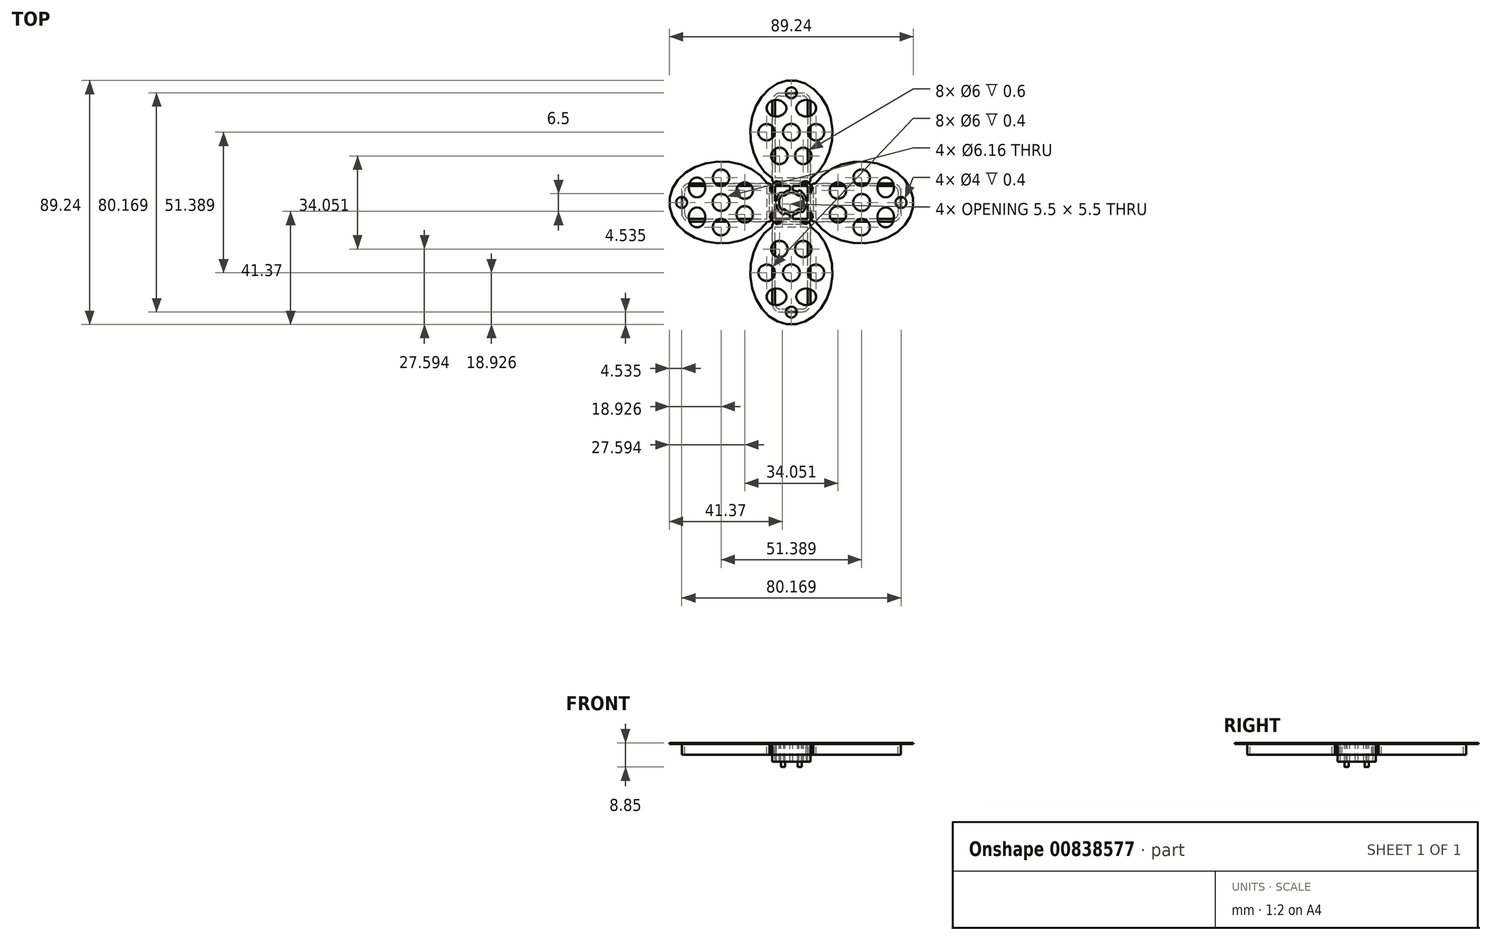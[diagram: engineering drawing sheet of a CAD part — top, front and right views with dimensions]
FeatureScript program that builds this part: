
annotation { "Feature Type Name" : "Feature", "Feature Type Description" : "" }
export const myFeature = defineFeature(function(context is Context, id is Id, definition is map)
    precondition{}
    {
        {
            var Q0;
            Q0=qCreatedBy(makeId("Top.planeOp"),FACE);
            var sketch = newSketch(context, id + "F0", { "sketchPlane" : qUnion([Q0])});
            skCircle(sketch, "E0", {"center": v(0, 0) * mm, "radius": 40 * mm, "construction": true});
            skLineSegment(sketch, "E1.bottom", {"start": v(40, 40) * mm, "end": v(-40, 40) * mm, "construction": true});
            skLineSegment(sketch, "E1.top", {"start": v(40, -40) * mm, "end": v(-40, -40) * mm, "construction": true});
            skLineSegment(sketch, "E1.left", {"start": v(40, 40) * mm, "end": v(40, -40) * mm, "construction": true});
            skLineSegment(sketch, "E1.right", {"start": v(-40, 40) * mm, "end": v(-40, -40) * mm, "construction": true});
            skLineSegment(sketch, "E2", {"start": v(0, 92.15) * mm, "end": v(0, -92.15) * mm, "construction": true});
            skLineSegment(sketch, "E3", {"start": v(-92.15, 0) * mm, "end": v(92.15, 0) * mm, "construction": true});
            skLineSegment(sketch, "E4", {"start": v(-92.15, 92.15) * mm, "end": v(92.15, -92.15) * mm, "construction": true});
            skLineSegment(sketch, "E5", {"start": v(92.15, 92.15) * mm, "end": v(-92.15, -92.15) * mm, "construction": true});
            skSolve(sketch);
        }
        {
            var Q0;
            Q0=qCreatedBy(makeId("Top.planeOp"),FACE);
            var sketch = newSketch(context, id + "F1", { "sketchPlane" : qUnion([Q0])});
            skLineSegment(sketch, "E6.bottom", {"start": v(7, 7) * mm, "end": v(-7, 7) * mm});
            skLineSegment(sketch, "E6.top", {"start": v(7, -7) * mm, "end": v(-7, -7) * mm});
            skLineSegment(sketch, "E6.left", {"start": v(7, 7) * mm, "end": v(7, -7) * mm});
            skLineSegment(sketch, "E6.right", {"start": v(-7, 7) * mm, "end": v(-7, -7) * mm});
            skPoint(sketch, "E6.middle", {"position": v(0, 0) * mm});
            skSolve(sketch);
        }
        {
            var Q0;
            Q0 = qSketchRegion(id + "F1", true);
            extrude(context, id + "F2", {"entities" : qUnion([Q0]), "oppositeDirection" : true, "depth" : 6.45 * mm, "offsetDistance" : 25 * mm});
        }
        {
            var Q0;
            Q0=qCreatedBy(makeId("Top.planeOp"),FACE);
            var sketch = newSketch(context, id + "F3", { "sketchPlane" : qUnion([Q0])});
            skLineSegment(sketch, "E7.bottom", {"start": v(7, 7) * mm, "end": v(-7, 7) * mm});
            skLineSegment(sketch, "E7.top", {"start": v(7, 40) * mm, "end": v(-7, 40) * mm});
            skLineSegment(sketch, "E7.left", {"start": v(7, 7) * mm, "end": v(7, 40) * mm});
            skLineSegment(sketch, "E7.right", {"start": v(-7, 7) * mm, "end": v(-7, 40) * mm});
            skPoint(sketch, "E7.middle", {"position": v(0, 23.5) * mm});
            skLineSegment(sketch, "E8.1.0", {"start": v(-7, 7) * mm, "end": v(-40, 7) * mm});
            skLineSegment(sketch, "E8.1.1", {"start": v(-7, 7) * mm, "end": v(-7, -7) * mm});
            skPoint(sketch, "E8.1.2", {"position": v(-23.5, 0) * mm});
            skLineSegment(sketch, "E8.1.3", {"start": v(-7, -7) * mm, "end": v(-40, -7) * mm});
            skLineSegment(sketch, "E8.1.4", {"start": v(-40, 7) * mm, "end": v(-40, -7) * mm});
            skLineSegment(sketch, "E8.2.0", {"start": v(-7, -7) * mm, "end": v(-7, -40) * mm});
            skLineSegment(sketch, "E8.2.1", {"start": v(-7, -7) * mm, "end": v(7, -7) * mm});
            skPoint(sketch, "E8.2.2", {"position": v(0, -23.5) * mm});
            skLineSegment(sketch, "E8.2.3", {"start": v(7, -7) * mm, "end": v(7, -40) * mm});
            skLineSegment(sketch, "E8.2.4", {"start": v(-7, -40) * mm, "end": v(7, -40) * mm});
            skLineSegment(sketch, "E8.3.0", {"start": v(7, -7) * mm, "end": v(40, -7) * mm});
            skLineSegment(sketch, "E8.3.1", {"start": v(7, -7) * mm, "end": v(7, 7) * mm});
            skPoint(sketch, "E8.3.2", {"position": v(23.5, 0) * mm});
            skLineSegment(sketch, "E8.3.3", {"start": v(7, 7) * mm, "end": v(40, 7) * mm});
            skLineSegment(sketch, "E8.3.4", {"start": v(40, -7) * mm, "end": v(40, 7) * mm});
            skPoint(sketch, "E8.center", {"position": v(0, 0) * mm});
            skSolve(sketch);
        }
        {
            var Q0;
            Q0 = qSketchRegion(id + "F3", true);
            extrude(context, id + "F4", {"entities" : qUnion([Q0]), "operationType" : NewBodyOperationType.ADD, "oppositeDirection" : true, "depth" : .2 * mm, "offsetDistance" : 25 * mm});
        }
        {
            var Q0;
            Q0=qCreatedBy(makeId("Top.planeOp"),FACE);
            var sketch = newSketch(context, id + "F5", { "sketchPlane" : qUnion([Q0])});
            skLineSegment(sketch, "E9.bottom", {"start": v(-7, -8) * mm, "end": v(-4.5, -8) * mm});
            skLineSegment(sketch, "E9.top", {"start": v(-7, -7) * mm, "end": v(-4.5, -7) * mm});
            skLineSegment(sketch, "E9.left", {"start": v(-7, -8) * mm, "end": v(-7, -7) * mm});
            skLineSegment(sketch, "E9.right", {"start": v(-4.5, -8) * mm, "end": v(-4.5, -7) * mm});
            skLineSegment(sketch, "E10.MirrorCS", {"start": v(7, -8) * mm, "end": v(4.5, -8) * mm});
            skLineSegment(sketch, "E11.MirrorCS", {"start": v(4.5, -8) * mm, "end": v(4.5, -7) * mm});
            skLineSegment(sketch, "E12.MirrorCS", {"start": v(7, -7) * mm, "end": v(4.5, -7) * mm});
            skLineSegment(sketch, "E13.MirrorCS", {"start": v(7, -8) * mm, "end": v(7, -7) * mm});
            skLineSegment(sketch, "E14.1.0", {"start": v(7, 7) * mm, "end": v(7, 4.5) * mm});
            skLineSegment(sketch, "E14.1.1", {"start": v(7, -7) * mm, "end": v(7, -4.5) * mm});
            skLineSegment(sketch, "E14.1.2", {"start": v(8, 4.5) * mm, "end": v(7, 4.5) * mm});
            skLineSegment(sketch, "E14.1.3", {"start": v(8, -7) * mm, "end": v(7, -7) * mm});
            skLineSegment(sketch, "E14.1.4", {"start": v(8, 7) * mm, "end": v(8, 4.5) * mm});
            skLineSegment(sketch, "E14.1.5", {"start": v(8, 7) * mm, "end": v(7, 7) * mm});
            skLineSegment(sketch, "E14.1.6", {"start": v(8, -4.5) * mm, "end": v(7, -4.5) * mm});
            skLineSegment(sketch, "E14.1.7", {"start": v(8, -7) * mm, "end": v(8, -4.5) * mm});
            skLineSegment(sketch, "E14.2.0", {"start": v(-7, 7) * mm, "end": v(-4.5, 7) * mm});
            skLineSegment(sketch, "E14.2.1", {"start": v(7, 7) * mm, "end": v(4.5, 7) * mm});
            skLineSegment(sketch, "E14.2.2", {"start": v(-4.5, 8) * mm, "end": v(-4.5, 7) * mm});
            skLineSegment(sketch, "E14.2.3", {"start": v(7, 8) * mm, "end": v(7, 7) * mm});
            skLineSegment(sketch, "E14.2.4", {"start": v(-7, 8) * mm, "end": v(-4.5, 8) * mm});
            skLineSegment(sketch, "E14.2.5", {"start": v(-7, 8) * mm, "end": v(-7, 7) * mm});
            skLineSegment(sketch, "E14.2.6", {"start": v(4.5, 8) * mm, "end": v(4.5, 7) * mm});
            skLineSegment(sketch, "E14.2.7", {"start": v(7, 8) * mm, "end": v(4.5, 8) * mm});
            skLineSegment(sketch, "E14.3.0", {"start": v(-7, -7) * mm, "end": v(-7, -4.5) * mm});
            skLineSegment(sketch, "E14.3.1", {"start": v(-7, 7) * mm, "end": v(-7, 4.5) * mm});
            skLineSegment(sketch, "E14.3.2", {"start": v(-8, -4.5) * mm, "end": v(-7, -4.5) * mm});
            skLineSegment(sketch, "E14.3.3", {"start": v(-8, 7) * mm, "end": v(-7, 7) * mm});
            skLineSegment(sketch, "E14.3.4", {"start": v(-8, -7) * mm, "end": v(-8, -4.5) * mm});
            skLineSegment(sketch, "E14.3.5", {"start": v(-8, -7) * mm, "end": v(-7, -7) * mm});
            skLineSegment(sketch, "E14.3.6", {"start": v(-8, 4.5) * mm, "end": v(-7, 4.5) * mm});
            skLineSegment(sketch, "E14.3.7", {"start": v(-8, 7) * mm, "end": v(-8, 4.5) * mm});
            skPoint(sketch, "E14.center", {"position": v(0, 0) * mm});
            skSolve(sketch);
        }
        {
            var Q0;
            Q0 = qSketchRegion(id + "F5", true);
            var Q1;
            {var subQ0=sQuery(id+"F3.wireOp",EDGE,"E8.2.0");var subQ2=sQuery(id+"F3.wireOp",EDGE,"E8.1.3");var subQ4=sQuery(id+"F3.wireOp",EDGE,"E8.1.0");var subQ6=makeQuery(id+"F2.opExtrude","SWEPT_FACE",FACE,{"disambiguationData":[OSD([sQuery(id+"F1.wireOp",EDGE,"E6.bottom")])]});var subQ7=sQuery(id+"F3.wireOp",EDGE,"E7.right");var subQ10=sQuery(id+"F3.wireOp",EDGE,"E8.1.4");var subQ11=makeQuery(id+"F4.opExtrude","CAP_FACE",FACE,{"disambiguationData":[OSD([sQuery(id+"F3.wireOp",EDGE,"E7.top"),sQuery(id+"F3.wireOp",EDGE,"E7.left"),subQ7,subQ4,subQ2,subQ10,subQ0,sQuery(id+"F3.wireOp",EDGE,"E8.2.3"),sQuery(id+"F3.wireOp",EDGE,"E8.2.4"),sQuery(id+"F3.wireOp",EDGE,"E8.3.0"),sQuery(id+"F3.wireOp",EDGE,"E8.3.3"),sQuery(id+"F3.wireOp",EDGE,"E8.3.4")])],"isStart":false});Q1=makeQuery(id+"F11.boolean.opBoolean","SPLIT",FACE,{"disambiguationData":[TD([subQ6])],"derivedFrom":makeQuery(id+"F4.boolean.opBoolean","SPLIT",FACE,{"disambiguationData":[TD([makeQuery(id+"F4.opExtrude","SWEPT_FACE",FACE,{"disambiguationData":[OSD([subQ10])]})])],"derivedFrom":subQ11})});}
            extrude(context, id + "F6", {"entities" : qUnion([Q0]), "operationType" : NewBodyOperationType.REMOVE, "endBound" : BoundingType.UP_TO_SURFACE, "oppositeDirection" : true, "depth" : 25 * mm, "endBoundEntityFace" : qUnion([Q1]), "offsetDistance" : 25 * mm});
        }
        {
            var Q0;
            Q0=qCreatedBy(makeId("Top.planeOp"),FACE);
            var sketch = newSketch(context, id + "F7", { "sketchPlane" : qUnion([Q0])});
            skEllipse(sketch, "E15", {"center": v(0, 25.62) * mm, "majorRadius": 16.56 * mm, "minorRadius": 14.13 * mm, "majorAxis": v(0, 1)});
            skEllipse(sketch, "E16.1.0", {"center": v(-25.62, 0) * mm, "majorRadius": 16.56 * mm, "minorRadius": 14.13 * mm, "majorAxis": v(-1, 0)});
            skEllipse(sketch, "E16.2.0", {"center": v(0, -25.62) * mm, "majorRadius": 16.56 * mm, "minorRadius": 14.13 * mm, "majorAxis": v(0, -1)});
            skEllipse(sketch, "E16.3.0", {"center": v(25.62, 0) * mm, "majorRadius": 16.56 * mm, "minorRadius": 14.13 * mm, "majorAxis": v(1, 0)});
            skPoint(sketch, "E16.center", {"position": v(0, 0) * mm});
            skLineSegment(sketch, "E17", {"start": v(-17.7, 25.62) * mm, "end": v(18.9, 25.62) * mm, "construction": true});
            skSolve(sketch);
        }
        {
            var Q0;
            Q0=qCreatedBy(makeId("Top.planeOp"),FACE);
            var sketch = newSketch(context, id + "F8", { "sketchPlane" : qUnion([Q0])});
            skCircle(sketch, "E18", {"center": v(-9.03, 25.7) * mm, "radius": 3 * mm});
            skArc(sketch, "E19", {"start": v(-6.35, 14.78) * mm, "mid": v(-1.36, 17.03) * mm, "end": v(-6.35, 19.27) * mm});
            skArc(sketch, "E20.MirrorC", {"start": v(6.35, 14.78) * mm, "mid": v(1.36, 17.03) * mm, "end": v(6.35, 19.27) * mm});
            skCircle(sketch, "E21.MirrorC", {"center": v(9.03, 25.7) * mm, "radius": 3 * mm});
            skCircle(sketch, "E22", {"center": v(0, 25.7) * mm, "radius": 3.08 * mm});
            skEllipse(sketch, "E23", {"center": v(-5.46, 34.49) * mm, "majorRadius": 3.63 * mm, "minorRadius": 3.04 * mm, "majorAxis": v(1, 0)});
            skEllipse(sketch, "E24.MirrorC", {"center": v(5.46, 34.49) * mm, "majorRadius": 3.63 * mm, "minorRadius": 3.04 * mm, "majorAxis": v(-1, 0)});
            skEllipse(sketch, "E25.MirrorC", {"center": v(5.46, 34.49) * mm, "majorRadius": 3.63 * mm, "minorRadius": 3.04 * mm, "majorAxis": v(-1, 0)});
            skLineSegment(sketch, "E26.left", {"start": v(6.35, 19.27) * mm, "end": v(6.35, 14.78) * mm});
            skLineSegment(sketch, "E26.right", {"start": v(-6.35, 19.27) * mm, "end": v(-6.35, 14.78) * mm});
            skPoint(sketch, "E26.middle", {"position": v(0, 16.86) * mm});
            skPoint(sketch, "E26.bottom.start.orphan", {"position": v(6.35, 20.86) * mm});
            skPoint(sketch, "E27.orphan", {"position": v(-6.35, 20.86) * mm});
            skPoint(sketch, "E28.orphan", {"position": v(-6.35, 12.86) * mm});
            skPoint(sketch, "E29.orphan", {"position": v(6.35, 12.86) * mm});
            skPoint(sketch, "E30.1.0", {"position": v(-16.86, 0) * mm});
            skArc(sketch, "E30.1.1", {"start": v(-14.78, -6.35) * mm, "mid": v(-17.03, -1.36) * mm, "end": v(-19.27, -6.35) * mm});
            skPoint(sketch, "E30.1.2", {"position": v(-20.86, 6.35) * mm});
            skEllipse(sketch, "E30.1.3", {"center": v(-34.49, -5.46) * mm, "majorRadius": 3.63 * mm, "minorRadius": 3.04 * mm, "majorAxis": v(0, 1)});
            skEllipse(sketch, "E30.1.4", {"center": v(-34.49, 5.46) * mm, "majorRadius": 3.63 * mm, "minorRadius": 3.04 * mm, "majorAxis": v(0, -1)});
            skPoint(sketch, "E30.1.5", {"position": v(-12.86, 6.35) * mm});
            skCircle(sketch, "E30.1.6", {"center": v(-25.7, 9.03) * mm, "radius": 3 * mm});
            skLineSegment(sketch, "E30.1.7", {"start": v(-19.27, 6.35) * mm, "end": v(-14.78, 6.35) * mm});
            skPoint(sketch, "E30.1.8", {"position": v(-12.86, -6.35) * mm});
            skLineSegment(sketch, "E30.1.9", {"start": v(-19.27, -6.35) * mm, "end": v(-14.78, -6.35) * mm});
            skCircle(sketch, "E30.1.10", {"center": v(-25.7, -9.03) * mm, "radius": 3 * mm});
            skPoint(sketch, "E30.1.11", {"position": v(-20.86, -6.35) * mm});
            skCircle(sketch, "E30.1.12", {"center": v(-25.7, 0) * mm, "radius": 3.08 * mm});
            skArc(sketch, "E30.1.13", {"start": v(-14.78, 6.35) * mm, "mid": v(-17.03, 1.36) * mm, "end": v(-19.27, 6.35) * mm});
            skEllipse(sketch, "E30.1.14", {"center": v(-34.49, 5.46) * mm, "majorRadius": 3.63 * mm, "minorRadius": 3.04 * mm, "majorAxis": v(0, -1)});
            skPoint(sketch, "E30.2.0", {"position": v(0, -16.86) * mm});
            skArc(sketch, "E30.2.1", {"start": v(6.35, -14.78) * mm, "mid": v(1.36, -17.03) * mm, "end": v(6.35, -19.27) * mm});
            skPoint(sketch, "E30.2.2", {"position": v(-6.35, -20.86) * mm});
            skEllipse(sketch, "E30.2.3", {"center": v(5.46, -34.49) * mm, "majorRadius": 3.63 * mm, "minorRadius": 3.04 * mm, "majorAxis": v(-1, 0)});
            skEllipse(sketch, "E30.2.4", {"center": v(-5.46, -34.49) * mm, "majorRadius": 3.63 * mm, "minorRadius": 3.04 * mm, "majorAxis": v(1, 0)});
            skPoint(sketch, "E30.2.5", {"position": v(-6.35, -12.86) * mm});
            skCircle(sketch, "E30.2.6", {"center": v(-9.03, -25.7) * mm, "radius": 3 * mm});
            skLineSegment(sketch, "E30.2.7", {"start": v(-6.35, -19.27) * mm, "end": v(-6.35, -14.78) * mm});
            skPoint(sketch, "E30.2.8", {"position": v(6.35, -12.86) * mm});
            skLineSegment(sketch, "E30.2.9", {"start": v(6.35, -19.27) * mm, "end": v(6.35, -14.78) * mm});
            skCircle(sketch, "E30.2.10", {"center": v(9.03, -25.7) * mm, "radius": 3 * mm});
            skPoint(sketch, "E30.2.11", {"position": v(6.35, -20.86) * mm});
            skCircle(sketch, "E30.2.12", {"center": v(0, -25.7) * mm, "radius": 3.08 * mm});
            skArc(sketch, "E30.2.13", {"start": v(-6.35, -14.78) * mm, "mid": v(-1.36, -17.03) * mm, "end": v(-6.35, -19.27) * mm});
            skEllipse(sketch, "E30.2.14", {"center": v(-5.46, -34.49) * mm, "majorRadius": 3.63 * mm, "minorRadius": 3.04 * mm, "majorAxis": v(1, 0)});
            skPoint(sketch, "E30.3.0", {"position": v(16.86, 0) * mm});
            skArc(sketch, "E30.3.1", {"start": v(14.78, 6.35) * mm, "mid": v(17.03, 1.36) * mm, "end": v(19.27, 6.35) * mm});
            skPoint(sketch, "E30.3.2", {"position": v(20.86, -6.35) * mm});
            skEllipse(sketch, "E30.3.3", {"center": v(34.49, 5.46) * mm, "majorRadius": 3.63 * mm, "minorRadius": 3.04 * mm, "majorAxis": v(0, -1)});
            skEllipse(sketch, "E30.3.4", {"center": v(34.49, -5.46) * mm, "majorRadius": 3.63 * mm, "minorRadius": 3.04 * mm, "majorAxis": v(0, 1)});
            skPoint(sketch, "E30.3.5", {"position": v(12.86, -6.35) * mm});
            skCircle(sketch, "E30.3.6", {"center": v(25.7, -9.03) * mm, "radius": 3 * mm});
            skLineSegment(sketch, "E30.3.7", {"start": v(19.27, -6.35) * mm, "end": v(14.78, -6.35) * mm});
            skPoint(sketch, "E30.3.8", {"position": v(12.86, 6.35) * mm});
            skLineSegment(sketch, "E30.3.9", {"start": v(19.27, 6.35) * mm, "end": v(14.78, 6.35) * mm});
            skCircle(sketch, "E30.3.10", {"center": v(25.7, 9.03) * mm, "radius": 3 * mm});
            skPoint(sketch, "E30.3.11", {"position": v(20.86, 6.35) * mm});
            skCircle(sketch, "E30.3.12", {"center": v(25.7, 0) * mm, "radius": 3.08 * mm});
            skArc(sketch, "E30.3.13", {"start": v(14.78, -6.35) * mm, "mid": v(17.03, -1.36) * mm, "end": v(19.27, -6.35) * mm});
            skEllipse(sketch, "E30.3.14", {"center": v(34.49, -5.46) * mm, "majorRadius": 3.63 * mm, "minorRadius": 3.04 * mm, "majorAxis": v(0, 1)});
            skPoint(sketch, "E30.center", {"position": v(0, 0) * mm});
            skSolve(sketch);
        }
        {
            var Q0;
            Q0 = qSketchRegion(id + "F8", true);
            var Q1;
            {var subQ0=sQuery(id+"F3.wireOp",EDGE,"E7.top");var subQ1=sQuery(id+"F3.wireOp",EDGE,"E7.left");var subQ2=sQuery(id+"F3.wireOp",EDGE,"E7.right");var subQ3=sQuery(id+"F3.wireOp",EDGE,"E8.3.3");var subQ4=sQuery(id+"F3.wireOp",EDGE,"E8.1.0");var subQ5=makeQuery(id+"F4.opExtrude","CAP_FACE",FACE,{"disambiguationData":[OSD([subQ0,subQ1,subQ2,subQ4,sQuery(id+"F3.wireOp",EDGE,"E8.1.3"),sQuery(id+"F3.wireOp",EDGE,"E8.1.4"),sQuery(id+"F3.wireOp",EDGE,"E8.2.0"),sQuery(id+"F3.wireOp",EDGE,"E8.2.3"),sQuery(id+"F3.wireOp",EDGE,"E8.2.4"),sQuery(id+"F3.wireOp",EDGE,"E8.3.0"),subQ3,sQuery(id+"F3.wireOp",EDGE,"E8.3.4")])],"isStart":false});Q1=makeQuery(id+"FxwcccIiPXIM7xx_1.boolean.opBoolean","MERGE",FACE,{"derivedFrom":[makeQuery(id+"F4.boolean.opBoolean","SPLIT",FACE,{"disambiguationData":[TD([makeQuery(id+"F4.opExtrude","SWEPT_FACE",FACE,{"disambiguationData":[OSD([subQ0])]})])],"derivedFrom":subQ5}),makeQuery(id+"FxwcccIiPXIM7xx_1.opExtrude","CAP_FACE",FACE,{"disambiguationData":[OSD([sQuery(id+"F7.wireOp",EDGE,"E15")])],"isStart":false})]});}
            extrude(context, id + "F9", {"entities" : qUnion([Q0]), "operationType" : NewBodyOperationType.REMOVE, "endBound" : BoundingType.UP_TO_SURFACE, "oppositeDirection" : true, "depth" : 25 * mm, "endBoundEntityFace" : qUnion([Q1]), "offsetDistance" : 25 * mm});
        }
        {
            var Q0;
            Q0=qCreatedBy(makeId("Top.planeOp"),FACE);
            var sketch = newSketch(context, id + "F10", { "sketchPlane" : qUnion([Q0])});
            skLineSegment(sketch, "E31.left", {"start": v(-7, -40) * mm, "end": v(-7, -8) * mm});
            skLineSegment(sketch, "E31.right", {"start": v(-6, -39) * mm, "end": v(-6, -9) * mm});
            skLineSegment(sketch, "E32.top", {"start": v(-6, -39) * mm, "end": v(0, -39) * mm});
            skLineSegment(sketch, "E33.top", {"start": v(-6, -9) * mm, "end": v(0, -9) * mm});
            skLineSegment(sketch, "E34", {"start": v(-7, -8) * mm, "end": v(-6.2, -7.2) * mm});
            skLineSegment(sketch, "E35", {"start": v(-6.2, -7.2) * mm, "end": v(-5.4, -8) * mm});
            skLineSegment(sketch, "E36.trimOffspring", {"start": v(-5.4, -8) * mm, "end": v(0, -8) * mm});
            skLineSegment(sketch, "E37", {"start": v(-7, -40) * mm, "end": v(0, -40) * mm});
            skLineSegment(sketch, "E38.MirrorCS", {"start": v(7, -8) * mm, "end": v(6.2, -7.2) * mm});
            skLineSegment(sketch, "E39.MirrorCS", {"start": v(7, -40) * mm, "end": v(7, -8) * mm});
            skLineSegment(sketch, "E40.MirrorCS", {"start": v(6, -39) * mm, "end": v(6, -9) * mm});
            skLineSegment(sketch, "E41.MirrorCS", {"start": v(5.4, -8) * mm, "end": v(0, -8) * mm});
            skLineSegment(sketch, "E42.MirrorCS", {"start": v(6.2, -7.2) * mm, "end": v(5.4, -8) * mm});
            skLineSegment(sketch, "E43.MirrorCS", {"start": v(7, -40) * mm, "end": v(0, -40) * mm});
            skLineSegment(sketch, "E44.MirrorCS", {"start": v(6, -9) * mm, "end": v(0, -9) * mm});
            skLineSegment(sketch, "E45.MirrorCS", {"start": v(6, -39) * mm, "end": v(0, -39) * mm});
            skLineSegment(sketch, "E46.1.0", {"start": v(8, -5.4) * mm, "end": v(8, 0) * mm});
            skLineSegment(sketch, "E46.1.1", {"start": v(40, 7) * mm, "end": v(8, 7) * mm});
            skLineSegment(sketch, "E46.1.2", {"start": v(8, 5.4) * mm, "end": v(8, 0) * mm});
            skLineSegment(sketch, "E46.1.3", {"start": v(40, -7) * mm, "end": v(8, -7) * mm});
            skLineSegment(sketch, "E46.1.4", {"start": v(39, -6) * mm, "end": v(9, -6) * mm});
            skLineSegment(sketch, "E46.1.5", {"start": v(9, 6) * mm, "end": v(9, 0) * mm});
            skLineSegment(sketch, "E46.1.6", {"start": v(39, 6) * mm, "end": v(9, 6) * mm});
            skLineSegment(sketch, "E46.1.7", {"start": v(40, 7) * mm, "end": v(40, 0) * mm});
            skLineSegment(sketch, "E46.1.8", {"start": v(39, 6) * mm, "end": v(39, 0) * mm});
            skLineSegment(sketch, "E46.1.9", {"start": v(9, -6) * mm, "end": v(9, 0) * mm});
            skLineSegment(sketch, "E46.1.10", {"start": v(39, -6) * mm, "end": v(39, 0) * mm});
            skLineSegment(sketch, "E46.1.11", {"start": v(40, -7) * mm, "end": v(40, 0) * mm});
            skLineSegment(sketch, "E46.1.12", {"start": v(7.2, 6.2) * mm, "end": v(8, 5.4) * mm});
            skLineSegment(sketch, "E46.1.13", {"start": v(8, -7) * mm, "end": v(7.2, -6.2) * mm});
            skLineSegment(sketch, "E46.1.14", {"start": v(8, 7) * mm, "end": v(7.2, 6.2) * mm});
            skLineSegment(sketch, "E46.1.15", {"start": v(7.2, -6.2) * mm, "end": v(8, -5.4) * mm});
            skLineSegment(sketch, "E46.2.0", {"start": v(5.4, 8) * mm, "end": v(0, 8) * mm});
            skLineSegment(sketch, "E46.2.1", {"start": v(-7, 40) * mm, "end": v(-7, 8) * mm});
            skLineSegment(sketch, "E46.2.2", {"start": v(-5.4, 8) * mm, "end": v(0, 8) * mm});
            skLineSegment(sketch, "E46.2.3", {"start": v(7, 40) * mm, "end": v(7, 8) * mm});
            skLineSegment(sketch, "E46.2.4", {"start": v(6, 39) * mm, "end": v(6, 9) * mm});
            skLineSegment(sketch, "E46.2.5", {"start": v(-6, 9) * mm, "end": v(0, 9) * mm});
            skLineSegment(sketch, "E46.2.6", {"start": v(-6, 39) * mm, "end": v(-6, 9) * mm});
            skLineSegment(sketch, "E46.2.7", {"start": v(-7, 40) * mm, "end": v(0, 40) * mm});
            skLineSegment(sketch, "E46.2.8", {"start": v(-6, 39) * mm, "end": v(0, 39) * mm});
            skLineSegment(sketch, "E46.2.9", {"start": v(6, 9) * mm, "end": v(0, 9) * mm});
            skLineSegment(sketch, "E46.2.10", {"start": v(6, 39) * mm, "end": v(0, 39) * mm});
            skLineSegment(sketch, "E46.2.11", {"start": v(7, 40) * mm, "end": v(0, 40) * mm});
            skLineSegment(sketch, "E46.2.12", {"start": v(-6.2, 7.2) * mm, "end": v(-5.4, 8) * mm});
            skLineSegment(sketch, "E46.2.13", {"start": v(7, 8) * mm, "end": v(6.2, 7.2) * mm});
            skLineSegment(sketch, "E46.2.14", {"start": v(-7, 8) * mm, "end": v(-6.2, 7.2) * mm});
            skLineSegment(sketch, "E46.2.15", {"start": v(6.2, 7.2) * mm, "end": v(5.4, 8) * mm});
            skLineSegment(sketch, "E46.3.0", {"start": v(-8, 5.4) * mm, "end": v(-8, 0) * mm});
            skLineSegment(sketch, "E46.3.1", {"start": v(-40, -7) * mm, "end": v(-8, -7) * mm});
            skLineSegment(sketch, "E46.3.2", {"start": v(-8, -5.4) * mm, "end": v(-8, 0) * mm});
            skLineSegment(sketch, "E46.3.3", {"start": v(-40, 7) * mm, "end": v(-8, 7) * mm});
            skLineSegment(sketch, "E46.3.4", {"start": v(-39, 6) * mm, "end": v(-9, 6) * mm});
            skLineSegment(sketch, "E46.3.5", {"start": v(-9, -6) * mm, "end": v(-9, 0) * mm});
            skLineSegment(sketch, "E46.3.6", {"start": v(-39, -6) * mm, "end": v(-9, -6) * mm});
            skLineSegment(sketch, "E46.3.7", {"start": v(-40, -7) * mm, "end": v(-40, 0) * mm});
            skLineSegment(sketch, "E46.3.8", {"start": v(-39, -6) * mm, "end": v(-39, 0) * mm});
            skLineSegment(sketch, "E46.3.9", {"start": v(-9, 6) * mm, "end": v(-9, 0) * mm});
            skLineSegment(sketch, "E46.3.10", {"start": v(-39, 6) * mm, "end": v(-39, 0) * mm});
            skLineSegment(sketch, "E46.3.11", {"start": v(-40, 7) * mm, "end": v(-40, 0) * mm});
            skLineSegment(sketch, "E46.3.12", {"start": v(-7.2, -6.2) * mm, "end": v(-8, -5.4) * mm});
            skLineSegment(sketch, "E46.3.13", {"start": v(-8, 7) * mm, "end": v(-7.2, 6.2) * mm});
            skLineSegment(sketch, "E46.3.14", {"start": v(-8, -7) * mm, "end": v(-7.2, -6.2) * mm});
            skLineSegment(sketch, "E46.3.15", {"start": v(-7.2, 6.2) * mm, "end": v(-8, 5.4) * mm});
            skPoint(sketch, "E46.center", {"position": v(0, 0) * mm});
            skSolve(sketch);
        }
        {
            var Q0;
            Q0 = qSketchRegion(id + "F10", true);
            extrude(context, id + "F11", {"entities" : qUnion([Q0]), "operationType" : NewBodyOperationType.ADD, "oppositeDirection" : true, "depth" : 4 * mm, "offsetDistance" : 25 * mm});
        }
        {
            var Q0;
            Q0=qCreatedBy(makeId("Top.planeOp"),FACE);
            var sketch = newSketch(context, id + "F12", { "sketchPlane" : qUnion([Q0])});
            skArc(sketch, "E47", {"start": v(-2.45, -2.5) * mm, "mid": v(0, -3.5) * mm, "end": v(2.45, -2.5) * mm});
            skArc(sketch, "E48", {"start": v(-3.74, 2.5) * mm, "mid": v(-4.5, 0) * mm, "end": v(-3.74, -2.5) * mm});
            skLineSegment(sketch, "E49.bottom", {"start": v(3.74, 2.5) * mm, "end": v(2.45, 2.5) * mm});
            skLineSegment(sketch, "E49.top", {"start": v(3.74, -2.5) * mm, "end": v(2.45, -2.5) * mm});
            skArc(sketch, "E50.trimOffspring", {"start": v(2.45, 2.5) * mm, "mid": v(0, 3.5) * mm, "end": v(-2.45, 2.5) * mm});
            skArc(sketch, "E51.trimOffspring", {"start": v(3.74, -2.5) * mm, "mid": v(4.5, 0) * mm, "end": v(3.74, 2.5) * mm});
            skLineSegment(sketch, "E52.trimOffspring", {"start": v(-2.45, -2.5) * mm, "end": v(-3.74, -2.5) * mm});
            skLineSegment(sketch, "E53.trimOffspring", {"start": v(-2.45, 2.5) * mm, "end": v(-3.74, 2.5) * mm});
            skSolve(sketch);
        }
        {
            var Q0;
            Q0 = qSketchRegion(id + "F12", true);
            var Q1;
            Q1=makeQuery(id+"F2.opExtrude","CAP_FACE",FACE,{"disambiguationData":[OSD([sQuery(id+"F1.wireOp",EDGE,"E6.bottom"),sQuery(id+"F1.wireOp",EDGE,"E6.top"),sQuery(id+"F1.wireOp",EDGE,"E6.left"),sQuery(id+"F1.wireOp",EDGE,"E6.right")])],"isStart":false});
            var Q2;
            Q2=makeQuery(id+"F4.opExtrude","CAP_FACE",FACE,{"disambiguationData":[OSD([sQuery(id+"F3.wireOp",EDGE,"E7.top"),sQuery(id+"F3.wireOp",EDGE,"E7.left"),sQuery(id+"F3.wireOp",EDGE,"E7.right"),sQuery(id+"F3.wireOp",EDGE,"E8.1.0"),sQuery(id+"F3.wireOp",EDGE,"E8.1.3"),sQuery(id+"F3.wireOp",EDGE,"E8.1.4"),sQuery(id+"F3.wireOp",EDGE,"E8.2.0"),sQuery(id+"F3.wireOp",EDGE,"E8.2.3"),sQuery(id+"F3.wireOp",EDGE,"E8.2.4"),sQuery(id+"F3.wireOp",EDGE,"E8.3.0"),sQuery(id+"F3.wireOp",EDGE,"E8.3.3"),sQuery(id+"F3.wireOp",EDGE,"E8.3.4")])],"isStart":false});
            extrude(context, id + "F13", {"entities" : qUnion([Q0]), "operationType" : NewBodyOperationType.REMOVE, "endBound" : BoundingType.UP_TO_SURFACE, "oppositeDirection" : true, "depth" : 25 * mm, "endBoundEntityFace" : qUnion([Q1]), "offsetDistance" : 25 * mm});
        }
        {
            var Q0;
            Q0=qCreatedBy(makeId("Top.planeOp"),FACE);
            var sketch = newSketch(context, id + "F14", { "sketchPlane" : qUnion([Q0])});
            skLineSegment(sketch, "E54.bottom", {"start": v(-7, -7) * mm, "end": v(7, -7) * mm});
            skLineSegment(sketch, "E54.top", {"start": v(-7, 7) * mm, "end": v(7, 7) * mm});
            skLineSegment(sketch, "E54.left", {"start": v(-7, -7) * mm, "end": v(-7, 7) * mm});
            skLineSegment(sketch, "E54.right", {"start": v(7, -7) * mm, "end": v(7, 7) * mm});
            skPoint(sketch, "E54.middle", {"position": v(0, 0) * mm});
            skSolve(sketch);
        }
        {
            var Q0;
            Q0 = qSketchRegion(id + "F14", true);
            extrude(context, id + "F15", {"entities" : qUnion([Q0]), "depth" : .4 * mm, "offsetDistance" : 25 * mm});
        }
        {
            var Q0;
            Q0=qCreatedBy(makeId("Top.planeOp"),FACE);
            var sketch = newSketch(context, id + "F16", { "sketchPlane" : qUnion([Q0])});
            skArc(sketch, "E55", {"start": v(2.47, 2.48) * mm, "mid": v(0, 3.5) * mm, "end": v(-2.47, 2.48) * mm});
            skArc(sketch, "E56", {"start": v(-3.75, 2.48) * mm, "mid": v(-4.5, 0) * mm, "end": v(-3.75, -2.48) * mm});
            skLineSegment(sketch, "E57.bottom", {"start": v(3.75, 2.48) * mm, "end": v(2.47, 2.48) * mm});
            skLineSegment(sketch, "E57.top", {"start": v(3.75, -2.48) * mm, "end": v(2.47, -2.48) * mm});
            skLineSegment(sketch, "E58.trimOffspring", {"start": v(-2.47, 2.48) * mm, "end": v(-3.75, 2.48) * mm});
            skArc(sketch, "E59.trimOffspring", {"start": v(-2.47, -2.48) * mm, "mid": v(0, -3.5) * mm, "end": v(2.47, -2.48) * mm});
            skLineSegment(sketch, "E60.trimOffspring", {"start": v(-2.47, -2.48) * mm, "end": v(-3.75, -2.48) * mm});
            skArc(sketch, "E61.trimOffspring", {"start": v(3.75, -2.48) * mm, "mid": v(4.5, 0) * mm, "end": v(3.75, 2.48) * mm});
            skSolve(sketch);
        }
        {
            var Q0;
            Q0 = qSketchRegion(id + "F16", true);
            var Q1;
            Q1=makeQuery(id+"F15.opExtrude","CAP_FACE",FACE,{"disambiguationData":[OSD([sQuery(id+"F14.wireOp",EDGE,"E54.bottom"),sQuery(id+"F14.wireOp",EDGE,"E54.top"),sQuery(id+"F14.wireOp",EDGE,"E54.left"),sQuery(id+"F14.wireOp",EDGE,"E54.right")])],"isStart":false});
            extrude(context, id + "F17", {"entities" : qUnion([Q0]), "operationType" : NewBodyOperationType.REMOVE, "endBound" : BoundingType.UP_TO_SURFACE, "depth" : 25 * mm, "endBoundEntityFace" : qUnion([Q1]), "offsetDistance" : 25 * mm});
        }
        {
            var Q0;
            Q0=qCreatedBy(makeId("Top.planeOp"),FACE);
            var sketch = newSketch(context, id + "F18", { "sketchPlane" : qUnion([Q0])});
            skEllipticalArc(sketch, "E62", {});
            skLineSegment(sketch, "E63.bottom", {"start": v(3, 5) * mm, "end": v(-3, 5) * mm});
            skLineSegment(sketch, "E63.left", {"start": v(3, 5) * mm, "end": v(3, 7) * mm});
            skLineSegment(sketch, "E63.right", {"start": v(-3, 5) * mm, "end": v(-3, 7) * mm});
            skPoint(sketch, "E63.middle", {"position": v(0, 6) * mm});
            skEllipticalArc(sketch, "E64.1.0", {});
            skLineSegment(sketch, "E64.1.1", {"start": v(-5, 3) * mm, "end": v(-5, -3) * mm});
            skLineSegment(sketch, "E64.1.2", {"start": v(-5, 3) * mm, "end": v(-7, 3) * mm});
            skLineSegment(sketch, "E64.1.3", {"start": v(-5, -3) * mm, "end": v(-7, -3) * mm});
            skPoint(sketch, "E64.1.4", {"position": v(-6, 0) * mm});
            skEllipticalArc(sketch, "E64.2.0", {});
            skLineSegment(sketch, "E64.2.1", {"start": v(-3, -5) * mm, "end": v(3, -5) * mm});
            skLineSegment(sketch, "E64.2.2", {"start": v(-3, -5) * mm, "end": v(-3, -7) * mm});
            skLineSegment(sketch, "E64.2.3", {"start": v(3, -5) * mm, "end": v(3, -7) * mm});
            skPoint(sketch, "E64.2.4", {"position": v(0, -6) * mm});
            skEllipticalArc(sketch, "E64.3.0", {});
            skLineSegment(sketch, "E64.3.1", {"start": v(5, -3) * mm, "end": v(5, 3) * mm});
            skLineSegment(sketch, "E64.3.2", {"start": v(5, -3) * mm, "end": v(7, -3) * mm});
            skLineSegment(sketch, "E64.3.3", {"start": v(5, 3) * mm, "end": v(7, 3) * mm});
            skPoint(sketch, "E64.3.4", {"position": v(6, 0) * mm});
            skPoint(sketch, "E64.center", {"position": v(0, 0) * mm});
            const initialGuessF18  = {"E62": [1.3584258448346135e-06, 0.025616473186351428, 1.669303998928029e-05, 0.9999999998606712, 0.019, 0.015, 3.342871326334596, 2.940155482730975], "E64.1.0": [-0.02561694140939603, 2.5291822014598953e-06, -0.9999999998606712, 1.6693039989096592e-05, 0.019, 0.015, 3.3428713263345955, 2.9401554827309746], "E64.2.0": [-2.9974052460657324e-06, -0.02561577065303941, -1.6693039989157826e-05, -0.9999999998606712, 0.019, 0.015, 3.3428713263345955, 2.9401554827309746], "E64.3.0": [0.025615302429994803, -1.8266488894364517e-06, 0.9999999998606712, -1.669303998897413e-05, 0.019, 0.015, 3.3428713263345955, 2.9401554827309746]};
            skSetInitialGuess(sketch, initialGuessF18);
            skSolve(sketch);
        }
        {
            var Q0;
            Q0 = qSketchRegion(id + "F18", true);
            extrude(context, id + "F19", {"entities" : qUnion([Q0]), "operationType" : NewBodyOperationType.ADD, "depth" : .4 * mm, "offsetDistance" : 25 * mm});
        }
        {
            var Q0;
            Q0=qCreatedBy(makeId("Top.planeOp"),FACE);
            var sketch = newSketch(context, id + "F20", { "sketchPlane" : qUnion([Q0])});
            skLineSegment(sketch, "E65", {"start": v(-7, 8.9) * mm, "end": v(-7, 8) * mm});
            skLineSegment(sketch, "E66", {"start": v(-7, 8) * mm, "end": v(-6.2, 7.2) * mm});
            skLineSegment(sketch, "E67", {"start": v(-6.2, 7.2) * mm, "end": v(-5.41, 7.99) * mm});
            skLineSegment(sketch, "E68", {"start": v(-5.41, 7.99) * mm, "end": v(-6.32, 8.9) * mm});
            skLineSegment(sketch, "E69", {"start": v(-6.32, 8.9) * mm, "end": v(-7, 8.9) * mm});
            skLineSegment(sketch, "E70.MirrorCS", {"start": v(7, 8.9) * mm, "end": v(7, 8) * mm});
            skLineSegment(sketch, "E71.MirrorCS", {"start": v(5.41, 7.99) * mm, "end": v(6.32, 8.9) * mm});
            skLineSegment(sketch, "E72.MirrorCS", {"start": v(7, 8) * mm, "end": v(6.2, 7.2) * mm});
            skLineSegment(sketch, "E73.MirrorCS", {"start": v(6.2, 7.2) * mm, "end": v(5.41, 7.99) * mm});
            skLineSegment(sketch, "E74.MirrorCS", {"start": v(6.32, 8.9) * mm, "end": v(7, 8.9) * mm});
            skLineSegment(sketch, "E75.1.0", {"start": v(-8.9, 7) * mm, "end": v(-8, 7) * mm});
            skLineSegment(sketch, "E75.1.1", {"start": v(-8.9, -7) * mm, "end": v(-8, -7) * mm});
            skLineSegment(sketch, "E75.1.2", {"start": v(-8.9, 6.32) * mm, "end": v(-8.9, 7) * mm});
            skLineSegment(sketch, "E75.1.3", {"start": v(-7.99, 5.41) * mm, "end": v(-8.9, 6.32) * mm});
            skLineSegment(sketch, "E75.1.4", {"start": v(-7.99, -5.41) * mm, "end": v(-8.9, -6.32) * mm});
            skLineSegment(sketch, "E75.1.5", {"start": v(-8.9, -6.32) * mm, "end": v(-8.9, -7) * mm});
            skLineSegment(sketch, "E75.1.6", {"start": v(-8, 7) * mm, "end": v(-7.2, 6.2) * mm});
            skLineSegment(sketch, "E75.1.7", {"start": v(-7.2, -6.2) * mm, "end": v(-7.99, -5.41) * mm});
            skLineSegment(sketch, "E75.1.8", {"start": v(-8, -7) * mm, "end": v(-7.2, -6.2) * mm});
            skLineSegment(sketch, "E75.1.9", {"start": v(-7.2, 6.2) * mm, "end": v(-7.99, 5.41) * mm});
            skLineSegment(sketch, "E75.2.0", {"start": v(-7, -8.9) * mm, "end": v(-7, -8) * mm});
            skLineSegment(sketch, "E75.2.1", {"start": v(7, -8.9) * mm, "end": v(7, -8) * mm});
            skLineSegment(sketch, "E75.2.2", {"start": v(-6.32, -8.9) * mm, "end": v(-7, -8.9) * mm});
            skLineSegment(sketch, "E75.2.3", {"start": v(-5.41, -7.99) * mm, "end": v(-6.32, -8.9) * mm});
            skLineSegment(sketch, "E75.2.4", {"start": v(5.41, -7.99) * mm, "end": v(6.32, -8.9) * mm});
            skLineSegment(sketch, "E75.2.5", {"start": v(6.32, -8.9) * mm, "end": v(7, -8.9) * mm});
            skLineSegment(sketch, "E75.2.6", {"start": v(-7, -8) * mm, "end": v(-6.2, -7.2) * mm});
            skLineSegment(sketch, "E75.2.7", {"start": v(6.2, -7.2) * mm, "end": v(5.41, -7.99) * mm});
            skLineSegment(sketch, "E75.2.8", {"start": v(7, -8) * mm, "end": v(6.2, -7.2) * mm});
            skLineSegment(sketch, "E75.2.9", {"start": v(-6.2, -7.2) * mm, "end": v(-5.41, -7.99) * mm});
            skLineSegment(sketch, "E75.3.0", {"start": v(8.9, -7) * mm, "end": v(8, -7) * mm});
            skLineSegment(sketch, "E75.3.1", {"start": v(8.9, 7) * mm, "end": v(8, 7) * mm});
            skLineSegment(sketch, "E75.3.2", {"start": v(8.9, -6.32) * mm, "end": v(8.9, -7) * mm});
            skLineSegment(sketch, "E75.3.3", {"start": v(7.99, -5.41) * mm, "end": v(8.9, -6.32) * mm});
            skLineSegment(sketch, "E75.3.4", {"start": v(7.99, 5.41) * mm, "end": v(8.9, 6.32) * mm});
            skLineSegment(sketch, "E75.3.5", {"start": v(8.9, 6.32) * mm, "end": v(8.9, 7) * mm});
            skLineSegment(sketch, "E75.3.6", {"start": v(8, -7) * mm, "end": v(7.2, -6.2) * mm});
            skLineSegment(sketch, "E75.3.7", {"start": v(7.2, 6.2) * mm, "end": v(7.99, 5.41) * mm});
            skLineSegment(sketch, "E75.3.8", {"start": v(8, 7) * mm, "end": v(7.2, 6.2) * mm});
            skLineSegment(sketch, "E75.3.9", {"start": v(7.2, -6.2) * mm, "end": v(7.99, -5.41) * mm});
            skPoint(sketch, "E75.center", {"position": v(0, 0) * mm});
            skSolve(sketch);
        }
        {
            var Q0;
            Q0 = qSketchRegion(id + "F20", true);
            extrude(context, id + "F21", {"entities" : qUnion([Q0]), "operationType" : NewBodyOperationType.ADD, "depth" : .4 * mm, "offsetDistance" : 25 * mm});
        }
        {
            var Q0;
            Q0=qCreatedBy(makeId("Top.planeOp"),FACE);
            var sketch = newSketch(context, id + "F22", { "sketchPlane" : qUnion([Q0])});
            skCircle(sketch, "E76", {"center": v(-9.03, 25.7) * mm, "radius": 3 * mm});
            skCircle(sketch, "E77.MirrorC", {"center": v(9.03, 25.7) * mm, "radius": 3 * mm});
            skCircle(sketch, "E78", {"center": v(0, 25.7) * mm, "radius": 3.08 * mm});
            skEllipse(sketch, "E79", {"center": v(-5.46, 34.49) * mm, "majorRadius": 3.63 * mm, "minorRadius": 3.04 * mm, "majorAxis": v(1, 0)});
            skEllipse(sketch, "E80.MirrorC", {"center": v(5.46, 34.49) * mm, "majorRadius": 3.63 * mm, "minorRadius": 3.04 * mm, "majorAxis": v(-1, 0)});
            skCircle(sketch, "E81", {"center": v(-4.36, 17.03) * mm, "radius": 3 * mm});
            skCircle(sketch, "E82", {"center": v(4.36, 17.03) * mm, "radius": 3 * mm});
            skCircle(sketch, "E83", {"center": v(0, 40.08) * mm, "radius": 2 * mm});
            skCircle(sketch, "E84.1.0", {"center": v(-40.08, 0) * mm, "radius": 2 * mm});
            skCircle(sketch, "E84.1.1", {"center": v(-17.03, -4.36) * mm, "radius": 3 * mm});
            skCircle(sketch, "E84.1.2", {"center": v(-25.7, 0) * mm, "radius": 3.08 * mm});
            skEllipse(sketch, "E84.1.3", {"center": v(-34.49, 5.46) * mm, "majorRadius": 3.63 * mm, "minorRadius": 3.04 * mm, "majorAxis": v(0, -1)});
            skCircle(sketch, "E84.1.4", {"center": v(-25.7, 9.03) * mm, "radius": 3 * mm});
            skCircle(sketch, "E84.1.5", {"center": v(-17.03, 4.36) * mm, "radius": 3 * mm});
            skCircle(sketch, "E84.1.6", {"center": v(-25.7, -9.03) * mm, "radius": 3 * mm});
            skEllipse(sketch, "E84.1.7", {"center": v(-34.49, -5.46) * mm, "majorRadius": 3.63 * mm, "minorRadius": 3.04 * mm, "majorAxis": v(0, 1)});
            skCircle(sketch, "E84.2.0", {"center": v(0, -40.08) * mm, "radius": 2 * mm});
            skCircle(sketch, "E84.2.1", {"center": v(4.36, -17.03) * mm, "radius": 3 * mm});
            skCircle(sketch, "E84.2.2", {"center": v(0, -25.7) * mm, "radius": 3.08 * mm});
            skEllipse(sketch, "E84.2.3", {"center": v(-5.46, -34.49) * mm, "majorRadius": 3.63 * mm, "minorRadius": 3.04 * mm, "majorAxis": v(1, 0)});
            skCircle(sketch, "E84.2.4", {"center": v(-9.03, -25.7) * mm, "radius": 3 * mm});
            skCircle(sketch, "E84.2.5", {"center": v(-4.36, -17.03) * mm, "radius": 3 * mm});
            skCircle(sketch, "E84.2.6", {"center": v(9.03, -25.7) * mm, "radius": 3 * mm});
            skEllipse(sketch, "E84.2.7", {"center": v(5.46, -34.49) * mm, "majorRadius": 3.63 * mm, "minorRadius": 3.04 * mm, "majorAxis": v(-1, 0)});
            skCircle(sketch, "E84.3.0", {"center": v(40.08, 0) * mm, "radius": 2 * mm});
            skCircle(sketch, "E84.3.1", {"center": v(17.03, 4.36) * mm, "radius": 3 * mm});
            skCircle(sketch, "E84.3.2", {"center": v(25.7, 0) * mm, "radius": 3.08 * mm});
            skEllipse(sketch, "E84.3.3", {"center": v(34.49, -5.46) * mm, "majorRadius": 3.63 * mm, "minorRadius": 3.04 * mm, "majorAxis": v(0, 1)});
            skCircle(sketch, "E84.3.4", {"center": v(25.7, -9.03) * mm, "radius": 3 * mm});
            skCircle(sketch, "E84.3.5", {"center": v(17.03, -4.36) * mm, "radius": 3 * mm});
            skCircle(sketch, "E84.3.6", {"center": v(25.7, 9.03) * mm, "radius": 3 * mm});
            skEllipse(sketch, "E84.3.7", {"center": v(34.49, 5.46) * mm, "majorRadius": 3.63 * mm, "minorRadius": 3.04 * mm, "majorAxis": v(0, -1)});
            skPoint(sketch, "E84.center", {"position": v(0, 0) * mm});
            skSolve(sketch);
        }
        {
            var Q0;
            Q0 = qSketchRegion(id + "F22", true);
            var Q1;
            Q1=makeQuery(id+"F19.opExtrude","CAP_FACE",FACE,{"disambiguationData":[OSD([sQuery(id+"F18.wireOp",EDGE,"E62"),sQuery(id+"F18.wireOp",EDGE,"E63.bottom"),sQuery(id+"F18.wireOp",EDGE,"E63.left"),sQuery(id+"F18.wireOp",EDGE,"E63.right")])],"isStart":false});
            extrude(context, id + "F23", {"entities" : qUnion([Q0]), "operationType" : NewBodyOperationType.REMOVE, "endBound" : BoundingType.UP_TO_SURFACE, "depth" : 25 * mm, "endBoundEntityFace" : qUnion([Q1]), "offsetDistance" : 25 * mm});
        }
        {
            var Q0;
            Q0=makeQuery(id+"F11.boolean.opBoolean","MERGE",EDGE,{"derivedFrom":[makeQuery(id+"F4.opExtrude","SWEPT_EDGE",EDGE,{"disambiguationData":[OSD([sQuery(id+"F3.wireOp",EDGE,"E7.top"),sQuery(id+"F3.wireOp",EDGE,"E7.left")])]}),makeQuery(id+"F11.opExtrude","SWEPT_EDGE",EDGE,{"disambiguationData":[OSD([sQuery(id+"F10.wireOp",EDGE,"E46.2.3"),sQuery(id+"F10.wireOp",EDGE,"E46.2.11")])]})]});
            var Q1;
            Q1=makeQuery(id+"F11.boolean.opBoolean","MERGE",EDGE,{"derivedFrom":[makeQuery(id+"F4.opExtrude","SWEPT_EDGE",EDGE,{"disambiguationData":[OSD([sQuery(id+"F3.wireOp",EDGE,"E7.top"),sQuery(id+"F3.wireOp",EDGE,"E7.right")])]}),makeQuery(id+"F11.opExtrude","SWEPT_EDGE",EDGE,{"disambiguationData":[OSD([sQuery(id+"F10.wireOp",EDGE,"E46.2.1"),sQuery(id+"F10.wireOp",EDGE,"E46.2.7")])]})]});
            var Q2;
            Q2=makeQuery(id+"F11.boolean.opBoolean","MERGE",EDGE,{"derivedFrom":[makeQuery(id+"F4.opExtrude","SWEPT_EDGE",EDGE,{"disambiguationData":[OSD([sQuery(id+"F3.wireOp",EDGE,"E8.1.0"),sQuery(id+"F3.wireOp",EDGE,"E8.1.4")])]}),makeQuery(id+"F11.opExtrude","SWEPT_EDGE",EDGE,{"disambiguationData":[OSD([sQuery(id+"F10.wireOp",EDGE,"E46.3.3"),sQuery(id+"F10.wireOp",EDGE,"E46.3.11")])]})]});
            var Q3;
            Q3=makeQuery(id+"F11.boolean.opBoolean","MERGE",EDGE,{"derivedFrom":[makeQuery(id+"F4.opExtrude","SWEPT_EDGE",EDGE,{"disambiguationData":[OSD([sQuery(id+"F3.wireOp",EDGE,"E8.1.3"),sQuery(id+"F3.wireOp",EDGE,"E8.1.4")])]}),makeQuery(id+"F11.opExtrude","SWEPT_EDGE",EDGE,{"disambiguationData":[OSD([sQuery(id+"F10.wireOp",EDGE,"E46.3.1"),sQuery(id+"F10.wireOp",EDGE,"E46.3.7")])]})]});
            var Q4;
            Q4=makeQuery(id+"F11.boolean.opBoolean","MERGE",EDGE,{"derivedFrom":[makeQuery(id+"F4.opExtrude","SWEPT_EDGE",EDGE,{"disambiguationData":[OSD([sQuery(id+"F3.wireOp",EDGE,"E8.2.0"),sQuery(id+"F3.wireOp",EDGE,"E8.2.4")])]}),makeQuery(id+"F11.opExtrude","SWEPT_EDGE",EDGE,{"disambiguationData":[OSD([sQuery(id+"F10.wireOp",EDGE,"E31.left"),sQuery(id+"F10.wireOp",EDGE,"E37")])]})]});
            var Q5;
            Q5=makeQuery(id+"F11.boolean.opBoolean","MERGE",EDGE,{"derivedFrom":[makeQuery(id+"F4.opExtrude","SWEPT_EDGE",EDGE,{"disambiguationData":[OSD([sQuery(id+"F3.wireOp",EDGE,"E8.2.3"),sQuery(id+"F3.wireOp",EDGE,"E8.2.4")])]}),makeQuery(id+"F11.opExtrude","SWEPT_EDGE",EDGE,{"disambiguationData":[OSD([sQuery(id+"F10.wireOp",EDGE,"E39.MirrorCS"),sQuery(id+"F10.wireOp",EDGE,"E43.MirrorCS")])]})]});
            var Q6;
            Q6=makeQuery(id+"F11.boolean.opBoolean","MERGE",EDGE,{"derivedFrom":[makeQuery(id+"F4.opExtrude","SWEPT_EDGE",EDGE,{"disambiguationData":[OSD([sQuery(id+"F3.wireOp",EDGE,"E8.3.0"),sQuery(id+"F3.wireOp",EDGE,"E8.3.4")])]}),makeQuery(id+"F11.opExtrude","SWEPT_EDGE",EDGE,{"disambiguationData":[OSD([sQuery(id+"F10.wireOp",EDGE,"E46.1.3"),sQuery(id+"F10.wireOp",EDGE,"E46.1.11")])]})]});
            var Q7;
            Q7=makeQuery(id+"F11.boolean.opBoolean","MERGE",EDGE,{"derivedFrom":[makeQuery(id+"F4.opExtrude","SWEPT_EDGE",EDGE,{"disambiguationData":[OSD([sQuery(id+"F3.wireOp",EDGE,"E8.3.3"),sQuery(id+"F3.wireOp",EDGE,"E8.3.4")])]}),makeQuery(id+"F11.opExtrude","SWEPT_EDGE",EDGE,{"disambiguationData":[OSD([sQuery(id+"F10.wireOp",EDGE,"E46.1.1"),sQuery(id+"F10.wireOp",EDGE,"E46.1.7")])]})]});
            fillet(context, id + "F24", {"entities" : qUnion([Q0, Q1, Q2, Q3, Q4, Q5, Q6, Q7]), "tangentPropagation" : true, "radius" : 3 * mm, "defaultsChanged" : false, "vertexSettings" : [], "allowEdgeOverflow" : false});
        }
        {
            var Q0;
            Q0=makeQuery(id+"F11.opExtrude","SWEPT_EDGE",EDGE,{"disambiguationData":[OSD([sQuery(id+"F10.wireOp",EDGE,"E46.1.6"),sQuery(id+"F10.wireOp",EDGE,"E46.1.8")])]});
            var Q1;
            Q1=makeQuery(id+"F11.opExtrude","SWEPT_EDGE",EDGE,{"disambiguationData":[OSD([sQuery(id+"F10.wireOp",EDGE,"E46.1.4"),sQuery(id+"F10.wireOp",EDGE,"E46.1.10")])]});
            var Q2;
            Q2=makeQuery(id+"F11.opExtrude","SWEPT_EDGE",EDGE,{"disambiguationData":[OSD([sQuery(id+"F10.wireOp",EDGE,"E46.2.4"),sQuery(id+"F10.wireOp",EDGE,"E46.2.10")])]});
            var Q3;
            Q3=makeQuery(id+"F11.opExtrude","SWEPT_EDGE",EDGE,{"disambiguationData":[OSD([sQuery(id+"F10.wireOp",EDGE,"E46.2.6"),sQuery(id+"F10.wireOp",EDGE,"E46.2.8")])]});
            var Q4;
            Q4=makeQuery(id+"F11.opExtrude","SWEPT_EDGE",EDGE,{"disambiguationData":[OSD([sQuery(id+"F10.wireOp",EDGE,"E46.3.4"),sQuery(id+"F10.wireOp",EDGE,"E46.3.10")])]});
            var Q5;
            Q5=makeQuery(id+"F11.opExtrude","SWEPT_EDGE",EDGE,{"disambiguationData":[OSD([sQuery(id+"F10.wireOp",EDGE,"E46.3.6"),sQuery(id+"F10.wireOp",EDGE,"E46.3.8")])]});
            var Q6;
            Q6=makeQuery(id+"F11.opExtrude","SWEPT_EDGE",EDGE,{"disambiguationData":[OSD([sQuery(id+"F10.wireOp",EDGE,"E31.right"),sQuery(id+"F10.wireOp",EDGE,"E32.top")])]});
            var Q7;
            Q7=makeQuery(id+"F11.opExtrude","SWEPT_EDGE",EDGE,{"disambiguationData":[OSD([sQuery(id+"F10.wireOp",EDGE,"E40.MirrorCS"),sQuery(id+"F10.wireOp",EDGE,"E45.MirrorCS")])]});
            fillet(context, id + "F25", {"entities" : qUnion([Q0, Q1, Q2, Q3, Q4, Q5, Q6, Q7]), "tangentPropagation" : true, "radius" : 2 * mm, "defaultsChanged" : false, "vertexSettings" : [], "allowEdgeOverflow" : false});
        }
        {
            var Q0;
            Q0=makeQuery(id+"F2.opExtrude","CAP_FACE",FACE,{"disambiguationData":[OSD([sQuery(id+"F1.wireOp",EDGE,"E6.bottom"),sQuery(id+"F1.wireOp",EDGE,"E6.top"),sQuery(id+"F1.wireOp",EDGE,"E6.left"),sQuery(id+"F1.wireOp",EDGE,"E6.right")])],"isStart":false});
            var sketch = newSketch(context, id + "F26", { "sketchPlane" : qUnion([Q0])});
            skCircle(sketch, "E85", {"center": v(3.04, -3.66) * mm, "radius": 0.75 * mm});
            skCircle(sketch, "E86.1.0", {"center": v(-3.04, 3.66) * mm, "radius": 0.75 * mm});
            skPoint(sketch, "E86.center", {"position": v(0, 0) * mm});
            skSolve(sketch);
        }
        {
            var Q0;
            Q0 = qSketchRegion(id + "F26", true);
            extrude(context, id + "F27", {"entities" : qUnion([Q0]), "operationType" : NewBodyOperationType.ADD, "depth" : 2 * mm, "offsetDistance" : 25 * mm});
        }
        {
            var Q0;
            Q0=qCreatedBy(makeId("Top.planeOp"),FACE);
            var sketch = newSketch(context, id + "F28", { "sketchPlane" : qUnion([Q0])});
            skLineSegment(sketch, "E87.bottom", {"start": v(6, -6) * mm, "end": v(0.5, -6) * mm});
            skLineSegment(sketch, "E87.left", {"start": v(6, -6) * mm, "end": v(6, -0.5) * mm});
            skLineSegment(sketch, "E87.right", {"start": v(-6, -6) * mm, "end": v(-6, -0.5) * mm});
            skArc(sketch, "E88", {"start": v(4.26, -3.48) * mm, "mid": v(5.1, -2.08) * mm, "end": v(5.48, -0.5) * mm});
            skLineSegment(sketch, "E89.bottom", {"start": v(-6, -0.5) * mm, "end": v(-5.48, -0.5) * mm});
            skLineSegment(sketch, "E90.left", {"start": v(-0.5, -6) * mm, "end": v(-0.5, -4.47) * mm});
            skLineSegment(sketch, "E90.right", {"start": v(0.5, -6) * mm, "end": v(0.5, -4.47) * mm});
            skLineSegment(sketch, "E91.bottom", {"start": v(-4.26, -3.48) * mm, "end": v(-3.78, -3.48) * mm});
            skLineSegment(sketch, "E92.trimOffspring", {"start": v(2.85, -3.48) * mm, "end": v(4.26, -3.48) * mm});
            skArc(sketch, "E93.trimOffspring", {"start": v(-2.32, -3.85) * mm, "mid": v(-1.44, -4.26) * mm, "end": v(-0.5, -4.47) * mm});
            skArc(sketch, "E94.trimOffspring", {"start": v(-5.48, -0.5) * mm, "mid": v(-5.1, -2.08) * mm, "end": v(-4.26, -3.48) * mm});
            skLineSegment(sketch, "E95.trimOffspring", {"start": v(5.48, -0.5) * mm, "end": v(6, -0.5) * mm});
            skArc(sketch, "E96.trimOffspring", {"start": v(0.5, -4.47) * mm, "mid": v(1.75, -4.15) * mm, "end": v(2.85, -3.48) * mm});
            skLineSegment(sketch, "E97.trimOffspring", {"start": v(-0.5, -6) * mm, "end": v(-6, -6) * mm});
            skLineSegment(sketch, "E98.MirrorCS", {"start": v(-6, 0.5) * mm, "end": v(-5.48, 0.5) * mm});
            skLineSegment(sketch, "E99.MirrorCS", {"start": v(6, 6) * mm, "end": v(6, 0.5) * mm});
            skLineSegment(sketch, "E100.MirrorCS", {"start": v(3.78, 3.48) * mm, "end": v(4.26, 3.48) * mm});
            skArc(sketch, "E101.MirrorCS", {"start": v(4.26, 3.48) * mm, "mid": v(5.1, 2.08) * mm, "end": v(5.48, 0.5) * mm});
            skLineSegment(sketch, "E102.MirrorCS", {"start": v(-0.5, 6) * mm, "end": v(-6, 6) * mm});
            skLineSegment(sketch, "E103.MirrorCS", {"start": v(-6, 6) * mm, "end": v(-6, 0.5) * mm});
            skLineSegment(sketch, "E104.MirrorCS", {"start": v(-4.26, 3.48) * mm, "end": v(-2.85, 3.48) * mm});
            skLineSegment(sketch, "E105.MirrorCS", {"start": v(-0.5, 6) * mm, "end": v(-0.5, 4.47) * mm});
            skLineSegment(sketch, "E106.MirrorCS", {"start": v(0.5, 6) * mm, "end": v(0.5, 4.47) * mm});
            skArc(sketch, "E107.MirrorCS", {"start": v(-2.85, 3.48) * mm, "mid": v(-1.75, 4.15) * mm, "end": v(-0.5, 4.47) * mm});
            skLineSegment(sketch, "E108.MirrorCS", {"start": v(6, 6) * mm, "end": v(0.5, 6) * mm});
            skLineSegment(sketch, "E109.MirrorCS", {"start": v(5.48, 0.5) * mm, "end": v(6, 0.5) * mm});
            skArc(sketch, "E110.MirrorCS", {"start": v(-5.48, 0.5) * mm, "mid": v(-5.1, 2.08) * mm, "end": v(-4.26, 3.48) * mm});
            skArc(sketch, "E111.MirrorCS", {"start": v(0.5, 4.47) * mm, "mid": v(1.44, 4.26) * mm, "end": v(2.32, 3.85) * mm});
            skArc(sketch, "E112", {"start": v(-3.78, -3.48) * mm, "mid": v(-3.23, -4.38) * mm, "end": v(-2.32, -3.85) * mm});
            skArc(sketch, "E113", {"start": v(3.78, 3.48) * mm, "mid": v(3.23, 4.38) * mm, "end": v(2.32, 3.85) * mm});
            skPoint(sketch, "E114.orphan", {"position": v(2.85, 3.48) * mm});
            skSolve(sketch);
        }
        {
            var Q0;
            Q0 = qSketchRegion(id + "F28", true);
            var Q1;
            Q1=makeQuery(id+"F2.opExtrude","CAP_FACE",FACE,{"disambiguationData":[OSD([sQuery(id+"F1.wireOp",EDGE,"E6.bottom"),sQuery(id+"F1.wireOp",EDGE,"E6.top"),sQuery(id+"F1.wireOp",EDGE,"E6.left"),sQuery(id+"F1.wireOp",EDGE,"E6.right")])],"isStart":false});
            var Q2;
            Q2=makeQuery(id+"F21.boolean.opBoolean","MERGE",FACE,{"derivedFrom":[makeQuery(id+"F19.boolean.opBoolean","MERGE",FACE,{"derivedFrom":[makeQuery(id+"F15.opExtrude","CAP_FACE",FACE,{"disambiguationData":[OSD([sQuery(id+"F14.wireOp",EDGE,"E54.bottom"),sQuery(id+"F14.wireOp",EDGE,"E54.top"),sQuery(id+"F14.wireOp",EDGE,"E54.left"),sQuery(id+"F14.wireOp",EDGE,"E54.right")])],"isStart":false}),makeQuery(id+"F19.opExtrude","CAP_FACE",FACE,{"disambiguationData":[OSD([sQuery(id+"F18.wireOp",EDGE,"E62"),sQuery(id+"F18.wireOp",EDGE,"E63.bottom"),sQuery(id+"F18.wireOp",EDGE,"E63.left"),sQuery(id+"F18.wireOp",EDGE,"E63.right")])],"isStart":false}),makeQuery(id+"F19.opExtrude","CAP_FACE",FACE,{"disambiguationData":[OSD([sQuery(id+"F18.wireOp",EDGE,"E64.1.0"),sQuery(id+"F18.wireOp",EDGE,"E64.1.1"),sQuery(id+"F18.wireOp",EDGE,"E64.1.2"),sQuery(id+"F18.wireOp",EDGE,"E64.1.3")])],"isStart":false}),makeQuery(id+"F19.opExtrude","CAP_FACE",FACE,{"disambiguationData":[OSD([sQuery(id+"F18.wireOp",EDGE,"E64.2.0"),sQuery(id+"F18.wireOp",EDGE,"E64.2.1"),sQuery(id+"F18.wireOp",EDGE,"E64.2.2"),sQuery(id+"F18.wireOp",EDGE,"E64.2.3")])],"isStart":false}),makeQuery(id+"F19.opExtrude","CAP_FACE",FACE,{"disambiguationData":[OSD([sQuery(id+"F18.wireOp",EDGE,"E64.3.0"),sQuery(id+"F18.wireOp",EDGE,"E64.3.1"),sQuery(id+"F18.wireOp",EDGE,"E64.3.2"),sQuery(id+"F18.wireOp",EDGE,"E64.3.3")])],"isStart":false})]}),makeQuery(id+"F21.opExtrude","CAP_FACE",FACE,{"disambiguationData":[OSD([sQuery(id+"F20.wireOp",EDGE,"E65"),sQuery(id+"F20.wireOp",EDGE,"E66"),sQuery(id+"F20.wireOp",EDGE,"E67"),sQuery(id+"F20.wireOp",EDGE,"E68"),sQuery(id+"F20.wireOp",EDGE,"E69")])],"isStart":false}),makeQuery(id+"F21.opExtrude","CAP_FACE",FACE,{"disambiguationData":[OSD([sQuery(id+"F20.wireOp",EDGE,"E70.MirrorCS"),sQuery(id+"F20.wireOp",EDGE,"E71.MirrorCS"),sQuery(id+"F20.wireOp",EDGE,"E72.MirrorCS"),sQuery(id+"F20.wireOp",EDGE,"E73.MirrorCS"),sQuery(id+"F20.wireOp",EDGE,"E74.MirrorCS")])],"isStart":false}),makeQuery(id+"F21.opExtrude","CAP_FACE",FACE,{"disambiguationData":[OSD([sQuery(id+"F20.wireOp",EDGE,"E75.1.0"),sQuery(id+"F20.wireOp",EDGE,"E75.1.2"),sQuery(id+"F20.wireOp",EDGE,"E75.1.3"),sQuery(id+"F20.wireOp",EDGE,"E75.1.6"),sQuery(id+"F20.wireOp",EDGE,"E75.1.9")])],"isStart":false}),makeQuery(id+"F21.opExtrude","CAP_FACE",FACE,{"disambiguationData":[OSD([sQuery(id+"F20.wireOp",EDGE,"E75.1.1"),sQuery(id+"F20.wireOp",EDGE,"E75.1.4"),sQuery(id+"F20.wireOp",EDGE,"E75.1.5"),sQuery(id+"F20.wireOp",EDGE,"E75.1.7"),sQuery(id+"F20.wireOp",EDGE,"E75.1.8")])],"isStart":false}),makeQuery(id+"F21.opExtrude","CAP_FACE",FACE,{"disambiguationData":[OSD([sQuery(id+"F20.wireOp",EDGE,"E75.2.0"),sQuery(id+"F20.wireOp",EDGE,"E75.2.2"),sQuery(id+"F20.wireOp",EDGE,"E75.2.3"),sQuery(id+"F20.wireOp",EDGE,"E75.2.6"),sQuery(id+"F20.wireOp",EDGE,"E75.2.9")])],"isStart":false}),makeQuery(id+"F21.opExtrude","CAP_FACE",FACE,{"disambiguationData":[OSD([sQuery(id+"F20.wireOp",EDGE,"E75.2.1"),sQuery(id+"F20.wireOp",EDGE,"E75.2.4"),sQuery(id+"F20.wireOp",EDGE,"E75.2.5"),sQuery(id+"F20.wireOp",EDGE,"E75.2.7"),sQuery(id+"F20.wireOp",EDGE,"E75.2.8")])],"isStart":false}),makeQuery(id+"F21.opExtrude","CAP_FACE",FACE,{"disambiguationData":[OSD([sQuery(id+"F20.wireOp",EDGE,"E75.3.0"),sQuery(id+"F20.wireOp",EDGE,"E75.3.2"),sQuery(id+"F20.wireOp",EDGE,"E75.3.3"),sQuery(id+"F20.wireOp",EDGE,"E75.3.6"),sQuery(id+"F20.wireOp",EDGE,"E75.3.9")])],"isStart":false}),makeQuery(id+"F21.opExtrude","CAP_FACE",FACE,{"disambiguationData":[OSD([sQuery(id+"F20.wireOp",EDGE,"E75.3.1"),sQuery(id+"F20.wireOp",EDGE,"E75.3.4"),sQuery(id+"F20.wireOp",EDGE,"E75.3.5"),sQuery(id+"F20.wireOp",EDGE,"E75.3.7"),sQuery(id+"F20.wireOp",EDGE,"E75.3.8")])],"isStart":false})]});
            extrude(context, id + "F29", {"entities" : qUnion([Q0]), "operationType" : NewBodyOperationType.REMOVE, "endBound" : BoundingType.UP_TO_SURFACE, "oppositeDirection" : true, "depth" : 25 * mm, "endBoundEntityFace" : qUnion([Q1]), "offsetDistance" : 25 * mm, "hasSecondDirection" : true, "secondDirectionBound" : SecondDirectionBoundingType.UP_TO_SURFACE, "secondDirectionOppositeDirection" : false, "secondDirectionDepth" : 25 * mm, "secondDirectionBoundEntityFace" : qUnion([Q2])});
        }
    });
